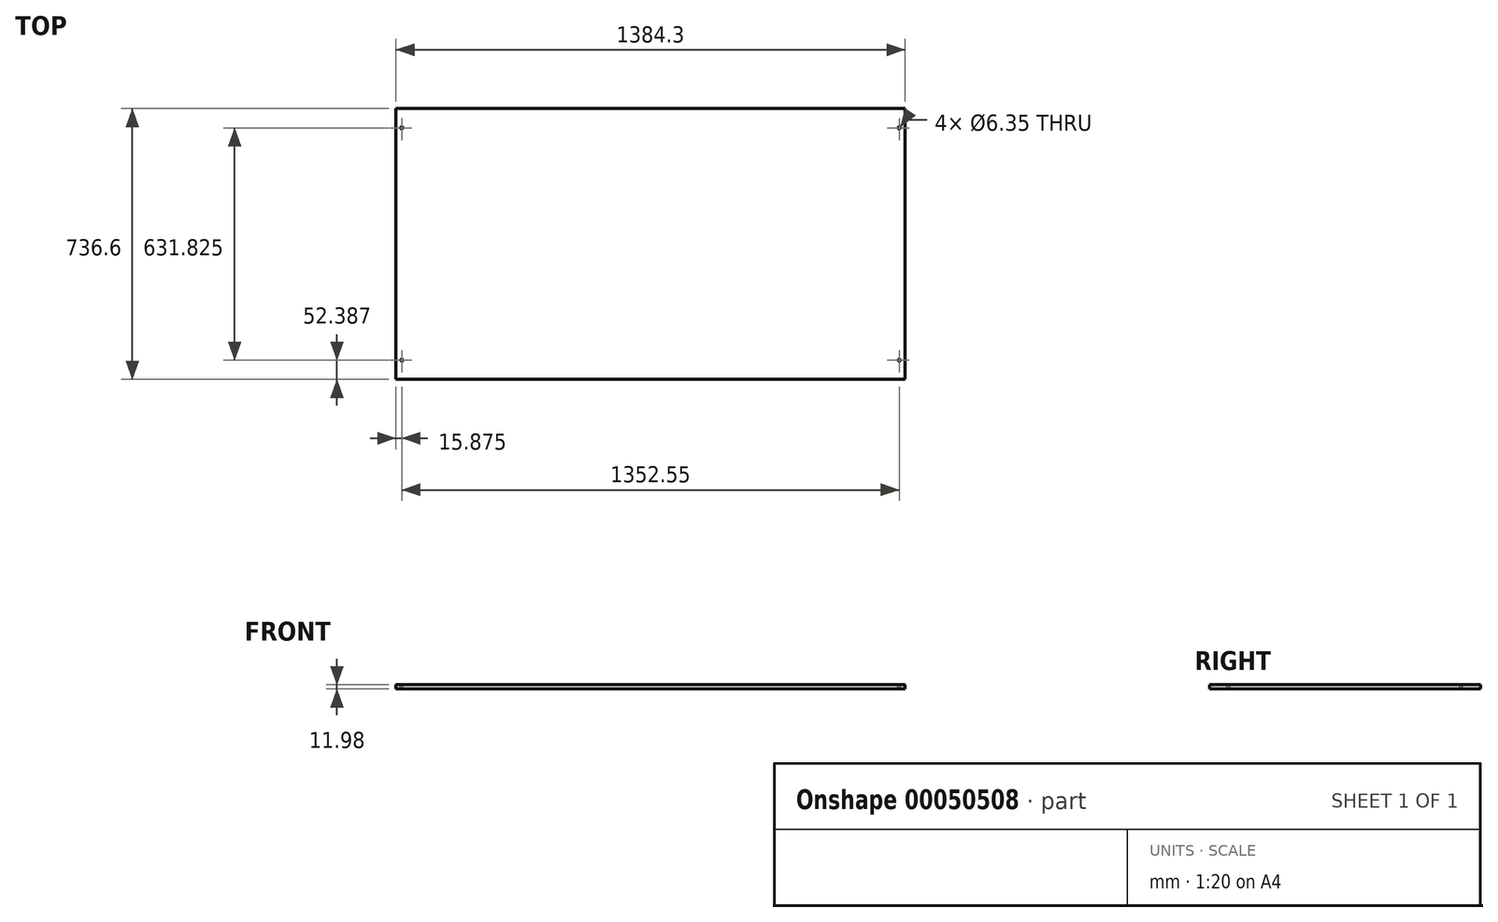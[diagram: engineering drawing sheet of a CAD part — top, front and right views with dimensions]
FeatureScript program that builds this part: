
annotation { "Feature Type Name" : "Feature", "Feature Type Description" : "" }
export const myFeature = defineFeature(function(context is Context, id is Id, definition is map)
    precondition{}
    {
        {
            var Q0;
            Q0=qCreatedBy(makeId("Top.planeOp"),FACE);
            var sketch = newSketch(context, id + "F0", { "sketchPlane" : qUnion([Q0])});
            skLineSegment(sketch, "E0.rect.bottom", {"start": v(692.15, 368.3) * mm, "end": v(-692.15, 368.3) * mm});
            skLineSegment(sketch, "E0.rect.top", {"start": v(692.15, -368.3) * mm, "end": v(-692.15, -368.3) * mm});
            skLineSegment(sketch, "E0.rect.left", {"start": v(692.15, 368.3) * mm, "end": v(692.15, -368.3) * mm});
            skLineSegment(sketch, "E0.rect.right", {"start": v(-692.15, 368.3) * mm, "end": v(-692.15, -368.3) * mm});
            skPoint(sketch, "E0.rect.middle", {"position": v(0, 0) * mm});
            skSolve(sketch);
        }
        {
            var Q0;
            Q0 = qSketchRegion(id + "F0", true);
            extrude(context, id + "F1", {"entities" : qUnion([Q0]), "endBound" : BoundingType.SYMMETRIC, "depth" : 12 * mm});
        }
        {
            var Q0;
            Q0=makeQuery(id+"F1.opExtrude","CAP_FACE",FACE,{"disambiguationData":[OSD([sQuery(id+"F0.wireOp",EDGE,"E0.rect.bottom"),sQuery(id+"F0.wireOp",EDGE,"E0.rect.top"),sQuery(id+"F0.wireOp",EDGE,"E0.rect.left"),sQuery(id+"F0.wireOp",EDGE,"E0.rect.right")])],"isStart":false});
            var sketch = newSketch(context, id + "F2", { "sketchPlane" : qUnion([Q0])});
            skLineSegment(sketch, "E1.rect.bottom", {"start": v(676.28, 315.91) * mm, "end": v(-676.28, 315.91) * mm, "construction": true});
            skLineSegment(sketch, "E1.rect.top", {"start": v(676.27, -315.91) * mm, "end": v(-676.27, -315.91) * mm, "construction": true});
            skLineSegment(sketch, "E1.rect.left", {"start": v(676.27, 315.91) * mm, "end": v(676.28, -315.91) * mm, "construction": true});
            skLineSegment(sketch, "E1.rect.right", {"start": v(-676.27, 315.91) * mm, "end": v(-676.27, -315.91) * mm, "construction": true});
            skCircle(sketch, "E2", {"center": v(-676.28, 315.91) * mm, "radius": 3.18 * mm});
            skCircle(sketch, "E3", {"center": v(676.28, 315.91) * mm, "radius": 3.18 * mm});
            skCircle(sketch, "E4", {"center": v(676.27, -315.91) * mm, "radius": 3.18 * mm});
            skCircle(sketch, "E5", {"center": v(-676.27, -315.91) * mm, "radius": 3.18 * mm});
            skLineSegment(sketch, "E6", {"start": v(0, -315.91) * mm, "end": v(0, 0) * mm, "construction": true});
            skSolve(sketch);
        }
        {
            var Q0;
            Q0 = qSketchRegion(id + "F2", true);
            extrude(context, id + "F3", {"entities" : qUnion([Q0]), "operationType" : NewBodyOperationType.REMOVE, "endBound" : BoundingType.UP_TO_NEXT, "oppositeDirection" : true, "depth" : 25.4 * mm});
        }
    });
